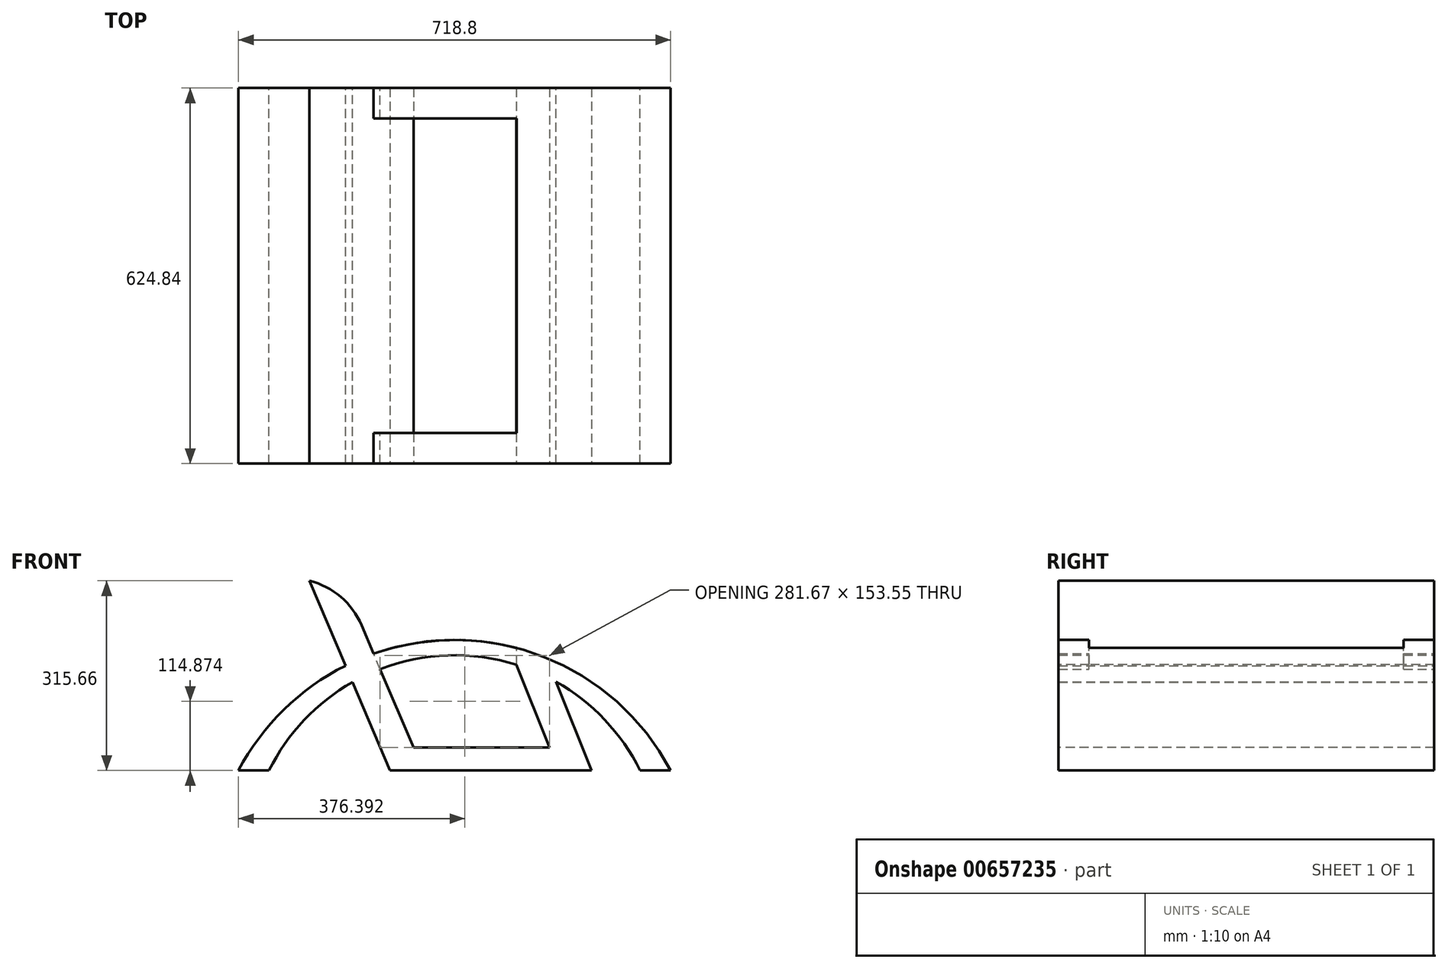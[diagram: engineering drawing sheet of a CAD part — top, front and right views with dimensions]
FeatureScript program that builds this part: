
annotation { "Feature Type Name" : "Feature", "Feature Type Description" : "" }
export const myFeature = defineFeature(function(context is Context, id is Id, definition is map)
    precondition{}
    {
        {
            var Q0;
            Q0=qCreatedBy(makeId("Front.planeOp"),FACE);
            var sketch = newSketch(context, id + "F0", { "sketchPlane" : qUnion([Q0])});
            skArc(sketch, "E0", {"start": v(359.4, -297.32) * mm, "mid": v(0, -80.1) * mm, "end": v(-359.4, -297.32) * mm});
            skArc(sketch, "E1", {"start": v(308.6, -297.32) * mm, "mid": v(0, -105.5) * mm, "end": v(-308.6, -297.32) * mm});
            skLineSegment(sketch, "E2", {"start": v(-359.4, -297.32) * mm, "end": v(-308.6, -297.32) * mm});
            skLineSegment(sketch, "E3", {"start": v(308.6, -297.32) * mm, "end": v(359.4, -297.32) * mm});
            skSolve(sketch);
        }
        {
            var Q0;
            Q0=qSketchRegion(id+"F0",true);
            extrude(context, id + "F1", {"entities" : qUnion([Q0]), "depth" : 624.84 * mm, "offsetDistance" : 25.4 * mm});
        }
        {
            var Q0;
            Q0=makeQuery(id+"F1.opExtrude","CAP_FACE",FACE,{"disambiguationData":[OSD([sQuery(id+"F0.wireOp",EDGE,"E0"),sQuery(id+"F0.wireOp",EDGE,"E1"),sQuery(id+"F0.wireOp",EDGE,"E2"),sQuery(id+"F0.wireOp",EDGE,"E3")])],"isStart":false});
            var sketch = newSketch(context, id + "F2", { "sketchPlane" : qUnion([Q0])});
            skLineSegment(sketch, "E4", {"start": v(-241.38, 18.34) * mm, "end": v(-107.4, -297.32) * mm});
            skLineSegment(sketch, "E5", {"start": v(-107.4, -297.32) * mm, "end": v(227.72, -297.32) * mm});
            skLineSegment(sketch, "E6", {"start": v(227.72, -297.32) * mm, "end": v(153.02, -110.04) * mm});
            skLineSegment(sketch, "E7", {"start": v(-68.38, -259.22) * mm, "end": v(157.83, -259.22) * mm});
            skLineSegment(sketch, "E8", {"start": v(157.83, -259.22) * mm, "end": v(102.78, -121.2) * mm});
            skLineSegment(sketch, "E9", {"start": v(102.78, -121.2) * mm, "end": v(153.02, -110.04) * mm});
            skLineSegment(sketch, "E10", {"start": v(-68.38, -259.22) * mm, "end": v(-154.8, -55.64) * mm});
            skArc(sketch, "E11", {"start": v(-154.8, -55.64) * mm, "mid": v(-189.38, -8.46) * mm, "end": v(-241.38, 18.34) * mm});
            skSolve(sketch);
        }
        {
            var Q0;
            Q0=qCreatedBy(makeId("Top.planeOp"),FACE);
            var sketch = newSketch(context, id + "F3", { "sketchPlane" : qUnion([Q0])});
            skLineSegment(sketch, "E12.bottom", {"start": v(-163.5, -50.8) * mm, "end": v(103.2, -50.8) * mm});
            skLineSegment(sketch, "E12.top", {"start": v(-163.5, -574.04) * mm, "end": v(103.2, -574.04) * mm});
            skLineSegment(sketch, "E12.left", {"start": v(-163.5, -50.8) * mm, "end": v(-163.5, -574.04) * mm});
            skLineSegment(sketch, "E12.right", {"start": v(103.2, -50.8) * mm, "end": v(103.2, -574.04) * mm});
            skSolve(sketch);
        }
        {
            var Q0;
            Q0=qSketchRegion(id+"F3",true);
            extrude(context, id + "F4", {"entities" : qUnion([Q0]), "operationType" : NewBodyOperationType.REMOVE, "oppositeDirection" : true, "depth" : 251.46 * mm, "offsetDistance" : 25.4 * mm});
        }
        {
            var Q0;
            Q0=qSketchRegion(id+"F2",true);
            extrude(context, id + "F5", {"entities" : qUnion([Q0]), "operationType" : NewBodyOperationType.ADD, "oppositeDirection" : true, "depth" : 624.84 * mm, "offsetDistance" : 25.4 * mm});
        }
    });
